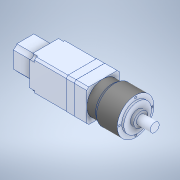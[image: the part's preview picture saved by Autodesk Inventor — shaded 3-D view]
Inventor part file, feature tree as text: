
AUTODESK INVENTOR PART (.ipt)
format: ipt  version: 2022 (Build 260153000, 153)  size: 236,032 bytes
history: mixed  units: in
note: dims shown in document units (in); Inventor stores cm internally (conversion verified against a paired STEP export)
features: extrude x4, sketch x4, other x1, imported_body x1
ambient origin geometry x8: Origin, YZ Plane, XZ Plane, XY Plane, X Axis, Y Axis, Z Axis, Center Point
bodies: Solid1 (imported_parasolid)
feature tree (10):
  extrude  "Extrusion1"  Depth=0.0197in
  extrude  "Extrusion2"  Depth=0.4724in
  extrude  "Extrusion3"  Depth=0.4724in
  extrude  "Extrusion4"  Depth=0.4724in
  sketch  "Sketch2"  dims[d8=0.7874in d9=0.0in d10=0.0197in]
  sketch  "Sketch3"  dims[d11=3.5433in d12=0.0in d13=0.4724in]
  sketch  "Sketch4"  dims[d14=0.4724in d15=0.4724in]
  sketch  "Sketch5"  dims[d16=0.4724in d17=0.4724in d18=0.0in d19=0.3937in d20=1.9685in d21=0.0in]
  other  "M6 Dişli Delik1"
  imported_body  NMx_Import_Brep_tag  [imported B-rep: ~66 faces, bbox_mm=[318.0, 80.0, 87.5]]
